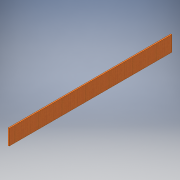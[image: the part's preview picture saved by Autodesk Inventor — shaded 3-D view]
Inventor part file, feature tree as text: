
AUTODESK INVENTOR PART (.ipt)
format: ipt  version: 2016 (Build 200138000, 138)  size: 93,696 bytes
history: native  units: in
note: dims shown in document units (in); Inventor stores cm internally (conversion verified against a paired STEP export)
features: extrude x1, sketch x1
ambient origin geometry x8: Origin, YZ Plane, XZ Plane, XY Plane, X Axis, Y Axis, Z Axis, Center Point
bodies: Solid1 (feature_tree)
feature tree (2):
  extrude  "Extrusion1"  Depth=6.5in
  sketch  "Sketch1"  dims[d0=69.0in d1=6.5in d2=0.4375in d3=0.0in]
